# Revit family: Storage_Tank-Rheem-Induro_Series--
name_source: partatom
category: Mechanical Equipment
units: mm (PartAtom-declared; Revit-internal decimal feet)

## family parameters
Always vertical = Yes
Classification = None
Cut with Voids When Loaded = No
OmniClass Number = 23.65.35.11.11
OmniClass Title = Storage Water Heaters
Part Type = Normal
Room Calculation Point = No
Round Connector Dimension = Use Diameter
Shared = No
Work Plane-Based = No

## types (1)
- 6N0325M0
    Assembly Code = D3020
    Base Mount Offset From Center = 220 mm  [stored 0.721785 ft]
    Cold Water Connection Size = 32 mm
    Cold Water Inlet Vertical Offset = 241 mm  [stored 0.790682 ft]
    Default Elevation = 0 mm  [stored 0 ft]
    Description = Storage Tank
    ENGworks Global = www.ENGworksGlobal.com
    Hot Water Connection Size = 32 mm
    Hot Water Flow Return Offset = 879 mm  [stored 2.88386 ft]
    Hot Water Outlet Vertical Offset = 1270 mm
    Manufacturer = Rheem
    Maximum DHW Pressure = 680.0 kPa
    Maximum Working Pressure = 1000.0 kPa
    Model = 6N0325M0
    Pipe Offset = 313 mm
    Primary Return Connection Size = 32 mm
    Primary Return Connection Vertical Offset = 200 mm  [stored 0.656168 ft]
    Product Page URL = https://www.rheem.com.au
    Series = INDURO
    TPR Valve Size = 20 mm
    TPR Valve Vertical Offset = 1290 mm  [stored 4.23228 ft]
    Tank Height = 1748 mm  [stored 5.73491 ft]
    Tank Material = Metal - Rheem - Stainless Steel
    Tank Outside Diameter = 621 mm  [stored 2.0374 ft]
    Tank Outside Radius = 311 mm
    Tank Volume = 325.00 L
    Top Hook Height = 110 mm  [stored 0.360892 ft]
    URL = https://www.rheem.com.au
    Unit Weight = 53.000 kgf
    Version = 1

note: [stored X ft] marks values corroborated as IEEE doubles in the binary element streams (Revit-internal decimal feet)

## geometry (parser evidence)
native form markers: Sweep x3
no freeform markers — native parametric forms only
